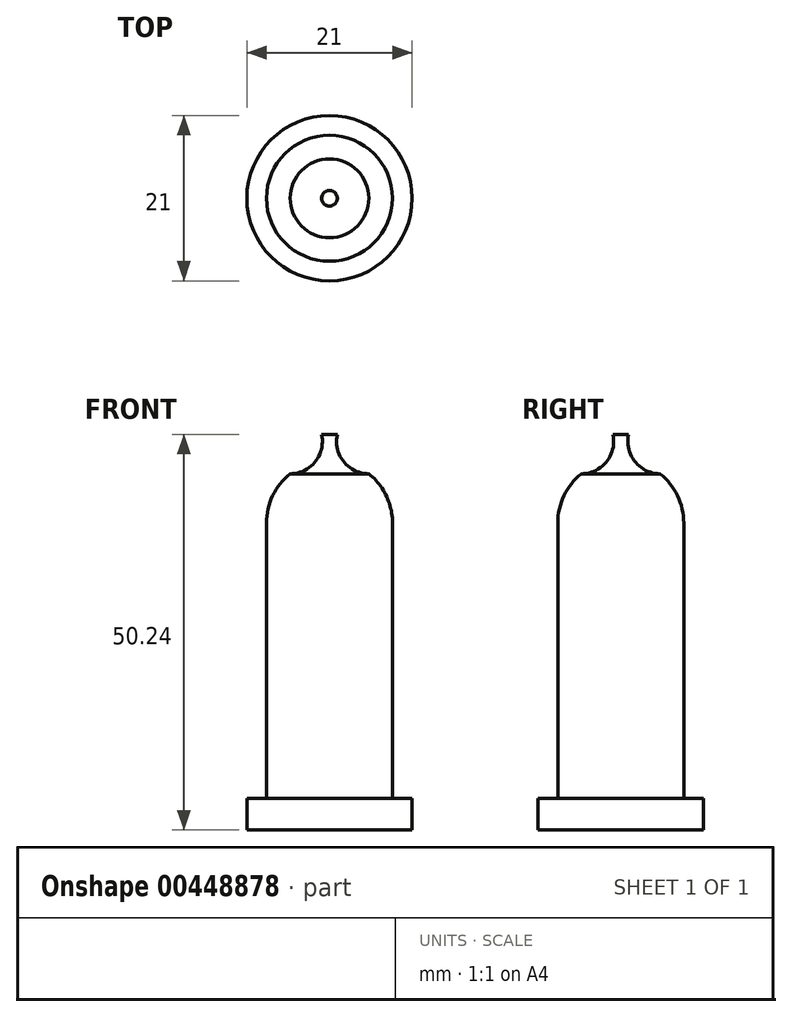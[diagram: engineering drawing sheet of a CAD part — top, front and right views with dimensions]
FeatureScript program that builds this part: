
annotation { "Feature Type Name" : "Feature", "Feature Type Description" : "" }
export const myFeature = defineFeature(function(context is Context, id is Id, definition is map)
    precondition{}
    {
        {
            var Q0;
            Q0=qCreatedBy(makeId("Top.planeOp"),FACE);
            var sketch = newSketch(context, id + "F0", { "sketchPlane" : qUnion([Q0])});
            skCircle(sketch, "E0", {"center": v(0, 0) * mm, "radius": 10.5 * mm});
            skSolve(sketch);
        }
        {
            var Q0;
            Q0=qSketchRegion(id+"F0",true);
            extrude(context, id + "F1", {"entities" : qUnion([Q0]), "depth" : 4 * mm});
        }
        {
            var Q0;
            Q0=qCreatedBy(makeId("Top.planeOp"),FACE);
            var sketch = newSketch(context, id + "F2", { "sketchPlane" : qUnion([Q0])});
            skCircle(sketch, "E1", {"center": v(0, 0) * mm, "radius": 8 * mm});
            skSolve(sketch);
        }
        {
            var Q0;
            Q0=qSketchRegion(id+"F2",true);
            extrude(context, id + "F3", {"entities" : qUnion([Q0]), "operationType" : NewBodyOperationType.ADD, "depth" : 39 * mm});
        }
        {
            var Q0;
            Q0=qCreatedBy(makeId("Right.planeOp"),FACE);
            var sketch = newSketch(context, id + "F4", { "sketchPlane" : qUnion([Q0])});
            skLineSegment(sketch, "E2", {"start": v(0, 47) * mm, "end": v(0, 39) * mm});
            skLineSegment(sketch, "E3", {"start": v(0, 39) * mm, "end": v(8, 39) * mm});
            skArc(sketch, "E4", {"start": v(8, 39) * mm, "mid": v(5.66, 44.66) * mm, "end": v(0, 47) * mm});
            skLineSegment(sketch, "E5", {"start": v(0, 45.24) * mm, "end": v(5, 45.24) * mm});
            skLineSegment(sketch, "E6", {"start": v(1, 50.24) * mm, "end": v(0, 50.24) * mm});
            skLineSegment(sketch, "E7", {"start": v(0, 50.24) * mm, "end": v(0, 45.24) * mm});
            skArc(sketch, "E8", {"start": v(1, 50.24) * mm, "mid": v(1.8, 46.78) * mm, "end": v(5, 45.24) * mm});
            skSolve(sketch);
        }
        {
            var Q0;
            Q0=makeQuery(id+"F4.imprint","IMPRINT",FACE,{"disambiguationData":[TD([[makeQuery(id+"F4.imprint","IMPRINT",EDGE,{"derivedFrom":sQuery(id+"F4.wireOp",EDGE,"E2")}),1.0]])]});
            var Q1;
            {var subQ4=sQuery(id+"F4.wireOp",EDGE,"E6");Q1=makeQuery(id+"F4.imprint","IMPRINT",FACE,{"disambiguationData":[TD([[makeQuery(id+"F4.imprint","IMPRINT",EDGE,{"derivedFrom":subQ4}),1.0]])]});}
            var Q2;
            {var subQ3=sQuery(id+"F4.wireOp",EDGE,"E5");Q2=makeQuery(id+"F4.imprint","IMPRINT",FACE,{"disambiguationData":[TD([[makeQuery(id+"F4.imprint","IMPRINT",EDGE,{"derivedFrom":subQ3}),1.0]])]});}
            var Q3;
            Q3=sQuery(id+"F4.wireOp",EDGE,"E2");
            revolve(context, id + "F5", {"operationType" : NewBodyOperationType.ADD, "entities" : qUnion([Q0, Q1, Q2]), "axis" : qUnion([Q3]), "revolveType" : RevolveType.FULL});
        }
    });
